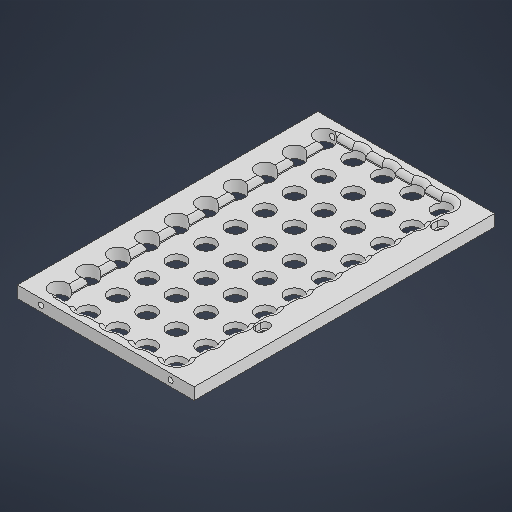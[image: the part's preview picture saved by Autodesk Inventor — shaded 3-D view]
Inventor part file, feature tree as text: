
AUTODESK INVENTOR PART (.ipt)
format: ipt  version: 2025.1 (Build 291241000, 241)  size: 1,013,248 bytes
history: native  units: in
note: dims shown in document units (in); Inventor stores cm internally (conversion verified against a paired STEP export)
features: extrude x7, sketch x7, plane x1, mirror x1, fillet x1, projected_geometry x1
ambient origin geometry x8: Origin, YZ Plane, XZ Plane, XY Plane, X Axis, Y Axis, Z Axis, Center Point
bodies: Solid1 (feature_tree)
feature tree (18):
  extrude  "Extrusion1"  Depth=0.3937in TaperAngle=0.0deg
  extrude  "Extrusion2"  Depth=0.7874in
  plane  "Work Plane1"
  mirror  "Mirror1"
  extrude  "Extrusion3"  Depth=0.1772in
  extrude  "Extrusion4"  Depth=0.3937in
  extrude  "Extrusion5"  Depth=5.9055in
  sketch  "Sketch6"  dims[d22=0.1772in d23=0.1772in d24=0.1772in d25=0.3937in d26=0.0in d27=0.315in d28=0.315in d29=0.315in d30=0.315in d31=0.1969in d32=0.0in d33=3.937in d34=9.252in d35=0.3937in d36=0.0in d37=0.5906in d39=1.1811in d40=3.937in d42=0.9843in d43=1.9685in d45=0.9843in d50=0.3937in d51=0.0in d52=3.6417in d53=0.0in d54=0.1575in d48=0.0197in d49=0.0344in]
  extrude  "Extrusion7"  Depth=0.1772in
  fillet  "Fillet1"  Radius=0.1772in
  extrude  "Extrusion8"  Depth=0.1575in
  sketch  "Sketch1"  dims[d0=5.9055in d1=10.0394in d2=0.3937in d3=3.6417in d4=0.3937in d5=0.315in d6=0.315in d7=0.3937in d8=0.0in]
  sketch  "Sketch2"  dims[d11=0.1772in d12=0.1772in]
  sketch  "Sketch3"  dims[d13=0.3937in d14=0.0in d15=1.2598in]
  sketch  "Sketch4"  dims[d16=0.5906in d17=5.9055in]
  projected_geometry  "Projected Loop1"
  sketch  "Sketch5"  dims[d19=0.1772in d20=0.1772in d21=0.1772in]
  sketch  "Sketch Rectangular Pattern1"  dims[d9=0.7874in d10=0.7874in]
